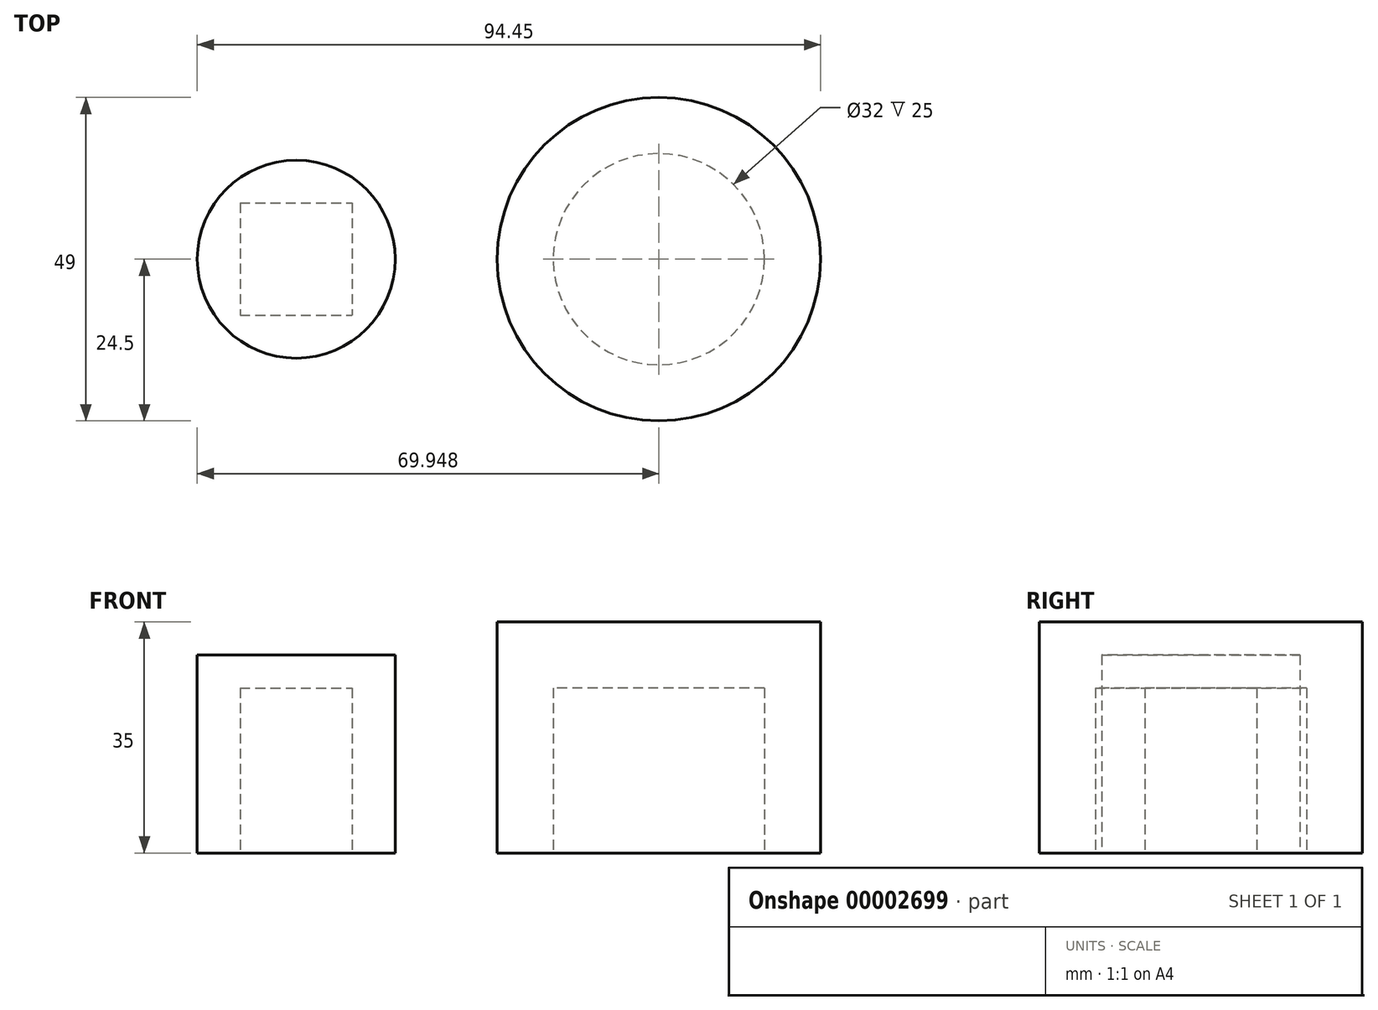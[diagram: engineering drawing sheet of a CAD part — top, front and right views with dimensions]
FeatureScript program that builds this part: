
annotation { "Feature Type Name" : "Feature", "Feature Type Description" : "" }
export const myFeature = defineFeature(function(context is Context, id is Id, definition is map)
    precondition{}
    {
        {
            var Q0;
            Q0=qCreatedBy(makeId("Top.planeOp"),FACE);
            var sketch = newSketch(context, id + "F0", { "sketchPlane" : qUnion([Q0])});
            skCircle(sketch, "E0", {"center": v(0, 0) * mm, "radius": 15 * mm});
            skLineSegment(sketch, "E1.bottom", {"start": v(-8.5, 8.5) * mm, "end": v(8.5, 8.5) * mm});
            skLineSegment(sketch, "E1.top", {"start": v(-8.5, -8.5) * mm, "end": v(8.5, -8.5) * mm});
            skLineSegment(sketch, "E1.left", {"start": v(-8.5, 8.5) * mm, "end": v(-8.5, -8.5) * mm});
            skLineSegment(sketch, "E1.right", {"start": v(8.5, 8.5) * mm, "end": v(8.5, -8.5) * mm});
            skPoint(sketch, "E2", {"position": v(0, 8.5) * mm});
            skPoint(sketch, "E3", {"position": v(8.5, 0) * mm});
            skSolve(sketch);
        }
        {
            var Q0;
            Q0 = qSketchRegion(id + "F0", true);
            var Q1;
            Q1=makeQuery(id+"F0.imprint","IMPRINT",FACE,{"disambiguationData":[TD([[makeQuery(id+"F0.imprint","IMPRINT",EDGE,{"derivedFrom":sQuery(id+"F0.wireOp",EDGE,"E1.bottom")}),-1.0]])]});
            extrude(context, id + "F1", {"entities" : qUnion([Q0, Q1]), "depth" : 30 * mm});
        }
        {
            var Q0;
            Q0=makeQuery(id+"F0.imprint","IMPRINT",FACE,{"disambiguationData":[TD([[makeQuery(id+"F0.imprint","IMPRINT",EDGE,{"derivedFrom":sQuery(id+"F0.wireOp",EDGE,"E1.bottom")}),-1.0]])]});
            extrude(context, id + "F2", {"entities" : qUnion([Q0]), "operationType" : NewBodyOperationType.REMOVE, "depth" : 25 * mm});
        }
        {
            var Q0;
            Q0=qCreatedBy(makeId("Top.planeOp"),FACE);
            var sketch = newSketch(context, id + "F3", { "sketchPlane" : qUnion([Q0])});
            skCircle(sketch, "E4", {"center": v(54.95, 0) * mm, "radius": 16 * mm});
            skCircle(sketch, "E5", {"center": v(54.95, 0) * mm, "radius": 24.5 * mm});
            skSolve(sketch);
        }
        {
            var Q0;
            Q0 = qSketchRegion(id + "F3", true);
            var Q1;
            Q1=makeQuery(id+"F3.imprint","IMPRINT",FACE,{"disambiguationData":[TD([[makeQuery(id+"F3.imprint","IMPRINT",EDGE,{"derivedFrom":sQuery(id+"F3.wireOp",EDGE,"E4")}),1.0]])]});
            extrude(context, id + "F4", {"entities" : qUnion([Q0, Q1]), "depth" : 35 * mm});
        }
        {
            var Q0;
            Q0=makeQuery(id+"F3.imprint","IMPRINT",FACE,{"disambiguationData":[TD([[makeQuery(id+"F3.imprint","IMPRINT",EDGE,{"derivedFrom":sQuery(id+"F3.wireOp",EDGE,"E4")}),1.0]])]});
            extrude(context, id + "F5", {"entities" : qUnion([Q0]), "operationType" : NewBodyOperationType.REMOVE, "depth" : 25 * mm});
        }
    });
